# Revit family: FU_Table_Sandler_512A-AX
name_source: partatom
category: Furniture
units: mm (PartAtom-declared; Revit-internal decimal feet)

## family parameters
Always vertical = Yes
Cut with Voids When Loaded = No
OmniClass Number = 23.40.20.00
OmniClass Title = General Furniture and Specialties
Room Calculation Point = No
Shared = No
Work Plane-Based = No

## types (3) — shared parameters
Depth = 600 mm  [stored 1.9685 ft]
Height = 1040 mm  [stored 3.41207 ft]
Manufacturer = Sandler
Model = 512A AX
Top Elevation = 1040 mm  [stored 3.41207 ft]
URL = https://www.sandlerseating.com
Width = 600 mm  [stored 1.9685 ft]
zero-valued in all types: Default Elevation

## per-type parameters (varying)
| type | Description | Top Size |
| 512A AX - 40" Round Top (100cm) | Table base. Available in powdercoat painted finishes. Optional upcharge for outdoor version with galvanized-treated frame and adjustable feet.
Optional upcharge for outdoor version with galvanized-treated frame and adjustable feet. | FU_TableTops_MT Rnd : 40" Round (100cm) |
| 512A AX - 36" Round Top (90cm) | Table base. Available in powdercoat painted finishes. Optional upcharge for outdoor version with galvanized-treated frame and adjustable feet.
Optional upcharge for outdoor version with galvanized-treated frame and adjustable feet. | FU_TableTops_MT Rnd : 36" Round (90cm) |
| 512A AX - 36" Square Top (90cm) | Table base. Available in powdercoat painted finishes.
Optional upcharge for outdoor version with galvanized-treated frame and adjustable feet. Optional upcharge for outdoor version with galvanized-treated frame and adjustable feet. | FU_TableTops_MT Sqr : 36" Square (90cm) |

note: [stored X ft] marks values corroborated as IEEE doubles in the binary element streams (Revit-internal decimal feet)

## geometry (parser evidence)
native form markers: Sweep x7
no freeform markers — native parametric forms only
